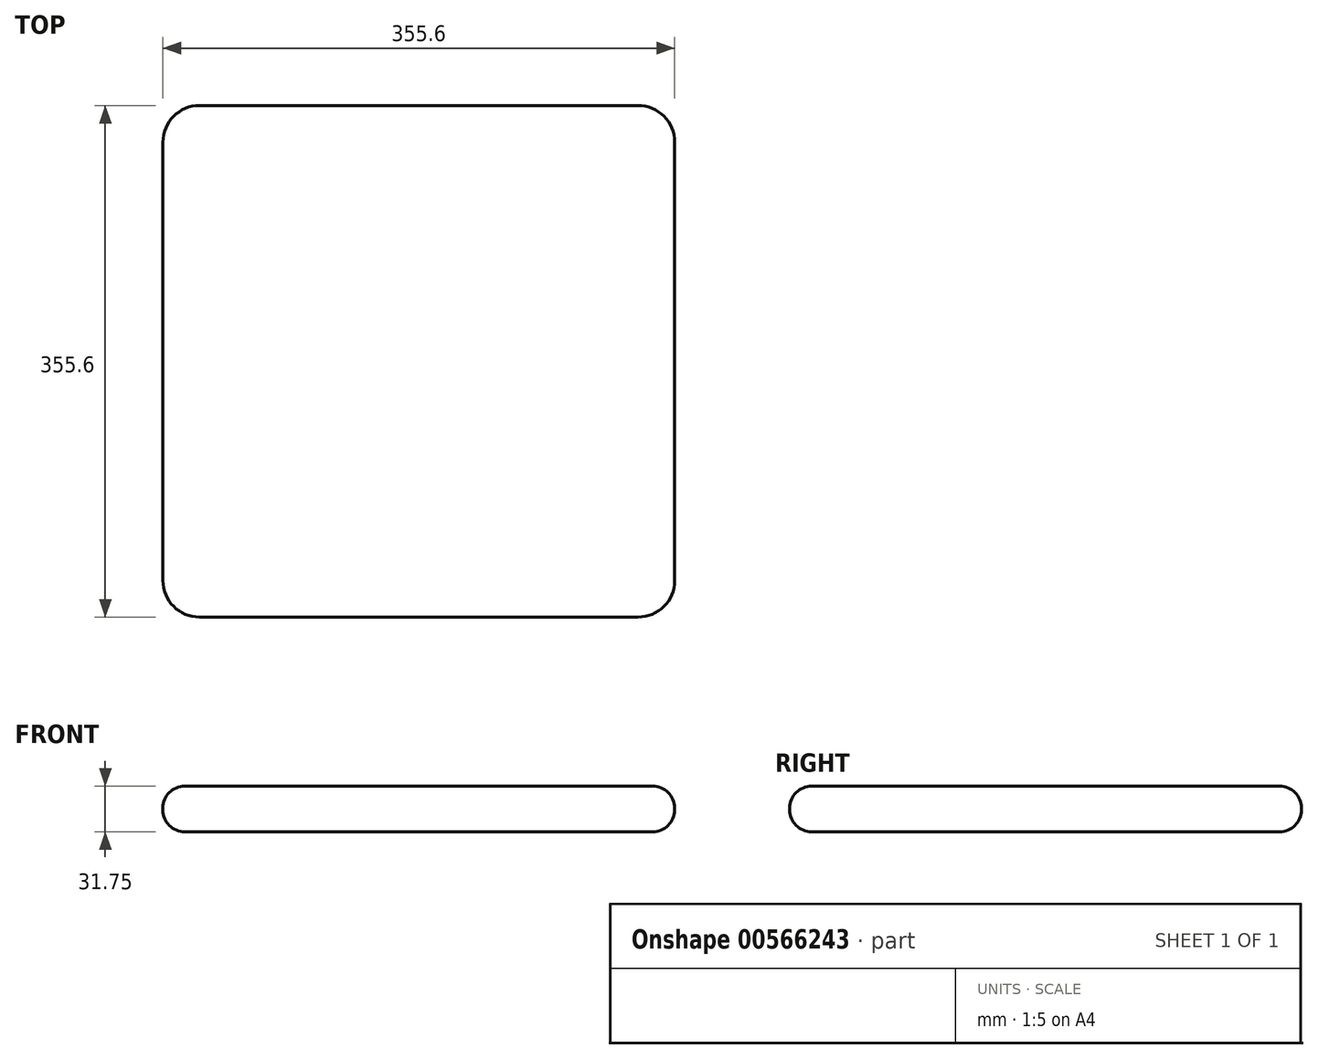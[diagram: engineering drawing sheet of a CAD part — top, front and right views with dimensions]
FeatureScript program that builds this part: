
annotation { "Feature Type Name" : "Feature", "Feature Type Description" : "" }
export const myFeature = defineFeature(function(context is Context, id is Id, definition is map)
    precondition{}
    {
        {
            var Q0;
            Q0=qCreatedBy(makeId("Top.planeOp"),FACE);
            var sketch = newSketch(context, id + "F0", { "sketchPlane" : qUnion([Q0])});
            skLineSegment(sketch, "E0.bottom", {"start": v(-152.4, 177.8) * mm, "end": v(152.4, 177.8) * mm});
            skLineSegment(sketch, "E0.top", {"start": v(-152.4, -177.8) * mm, "end": v(152.4, -177.8) * mm});
            skLineSegment(sketch, "E0.left", {"start": v(-177.8, 152.4) * mm, "end": v(-177.8, -152.4) * mm});
            skLineSegment(sketch, "E0.right", {"start": v(177.8, 152.4) * mm, "end": v(177.8, -152.4) * mm});
            skPoint(sketch, "E0.middle", {"position": v(0, 0) * mm});
            skPoint(sketch, "E1.visualSharp", {"position": v(-177.8, 177.8) * mm});
            skArc(sketch, "E1.filletArc", {"start": v(-152.4, 177.8) * mm, "mid": v(-170.36, 170.36) * mm, "end": v(-177.8, 152.4) * mm});
            skPoint(sketch, "E2.visualSharp", {"position": v(177.8, 177.8) * mm});
            skArc(sketch, "E2.filletArc", {"start": v(177.8, 152.4) * mm, "mid": v(170.36, 170.36) * mm, "end": v(152.4, 177.8) * mm});
            skPoint(sketch, "E3.visualSharp", {"position": v(-177.8, -177.8) * mm});
            skArc(sketch, "E3.filletArc", {"start": v(-177.8, -152.4) * mm, "mid": v(-170.36, -170.36) * mm, "end": v(-152.4, -177.8) * mm});
            skPoint(sketch, "E4.visualSharp", {"position": v(177.8, -177.8) * mm});
            skArc(sketch, "E4.filletArc", {"start": v(152.4, -177.8) * mm, "mid": v(170.36, -170.36) * mm, "end": v(177.8, -152.4) * mm});
            skSolve(sketch);
        }
        {
            var Q0;
            Q0=makeQuery(id+"F0.imprint","IMPRINT",FACE,{"disambiguationData":[TD([[makeQuery(id+"F0.imprint","IMPRINT",EDGE,{"derivedFrom":sQuery(id+"F0.wireOp",EDGE,"E0.bottom")}),-1.0]])]});
            extrude(context, id + "F1", {"entities" : qUnion([Q0]), "depth" : 31.75 * mm, "offsetDistance" : 25.4 * mm});
        }
        {
            var Q0;
            Q0=makeQuery(id+"F1.opExtrude","SWEPT_FACE",FACE,{"disambiguationData":[OSD([sQuery(id+"F0.wireOp",EDGE,"E0.bottom")])]});
            var Q1;
            Q1=makeQuery(id+"F1.opExtrude","CAP_FACE",FACE,{"disambiguationData":[OSD([sQuery(id+"F0.wireOp",EDGE,"E0.bottom"),sQuery(id+"F0.wireOp",EDGE,"E0.top"),sQuery(id+"F0.wireOp",EDGE,"E0.left"),sQuery(id+"F0.wireOp",EDGE,"E0.right"),sQuery(id+"F0.wireOp",EDGE,"E1.filletArc"),sQuery(id+"F0.wireOp",EDGE,"E2.filletArc"),sQuery(id+"F0.wireOp",EDGE,"E3.filletArc"),sQuery(id+"F0.wireOp",EDGE,"E4.filletArc")])],"isStart":false});
            var Q2;
            Q2=makeQuery(id+"F1.opExtrude","CAP_FACE",FACE,{"disambiguationData":[OSD([sQuery(id+"F0.wireOp",EDGE,"E0.bottom"),sQuery(id+"F0.wireOp",EDGE,"E0.top"),sQuery(id+"F0.wireOp",EDGE,"E0.left"),sQuery(id+"F0.wireOp",EDGE,"E0.right"),sQuery(id+"F0.wireOp",EDGE,"E1.filletArc"),sQuery(id+"F0.wireOp",EDGE,"E2.filletArc"),sQuery(id+"F0.wireOp",EDGE,"E3.filletArc"),sQuery(id+"F0.wireOp",EDGE,"E4.filletArc")])],"isStart":true});
            var Q3;
            Q3=makeQuery(id+"F1.opExtrude","SWEPT_FACE",FACE,{"disambiguationData":[OSD([sQuery(id+"F0.wireOp",EDGE,"E0.left")])]});
            var Q4;
            Q4=makeQuery(id+"F1.opExtrude","SWEPT_FACE",FACE,{"disambiguationData":[OSD([sQuery(id+"F0.wireOp",EDGE,"E0.right")])]});
            var Q5;
            Q5=makeQuery(id+"F1.opExtrude","CAP_EDGE",EDGE,{"disambiguationData":[OSD([sQuery(id+"F0.wireOp",EDGE,"E0.bottom")])],"isStart":true});
            var Q6;
            Q6=makeQuery(id+"F1.opExtrude","SWEPT_FACE",FACE,{"disambiguationData":[OSD([sQuery(id+"F0.wireOp",EDGE,"E3.filletArc")])]});
            var Q7;
            Q7=makeQuery(id+"F1.opExtrude","SWEPT_FACE",FACE,{"disambiguationData":[OSD([sQuery(id+"F0.wireOp",EDGE,"E0.top")])]});
            var Q8;
            Q8=makeQuery(id+"F1.opExtrude","SWEPT_FACE",FACE,{"disambiguationData":[OSD([sQuery(id+"F0.wireOp",EDGE,"E2.filletArc")])]});
            var Q9;
            Q9=makeQuery(id+"F1.opExtrude","CAP_EDGE",EDGE,{"disambiguationData":[OSD([sQuery(id+"F0.wireOp",EDGE,"E0.bottom")])],"isStart":false});
            var Q10;
            Q10=makeQuery(id+"F1.opExtrude","SWEPT_FACE",FACE,{"disambiguationData":[OSD([sQuery(id+"F0.wireOp",EDGE,"E1.filletArc")])]});
            var Q11;
            Q11=makeQuery(id+"F1.opExtrude","CAP_EDGE",EDGE,{"disambiguationData":[OSD([sQuery(id+"F0.wireOp",EDGE,"E2.filletArc")])],"isStart":false});
            var Q12;
            Q12=makeQuery(id+"F1.opExtrude","SWEPT_FACE",FACE,{"disambiguationData":[OSD([sQuery(id+"F0.wireOp",EDGE,"E4.filletArc")])]});
            var Q13;
            Q13=makeQuery(id+"F1.opExtrude","CAP_EDGE",EDGE,{"disambiguationData":[OSD([sQuery(id+"F0.wireOp",EDGE,"E0.left")])],"isStart":true});
            var Q14;
            Q14=makeQuery(id+"F1.opExtrude","SWEPT_EDGE",EDGE,{"disambiguationData":[OSD([sQuery(id+"F0.wireOp",EDGE,"E0.top"),sQuery(id+"F0.wireOp",EDGE,"E4.filletArc")])]});
            var Q15;
            Q15=makeQuery(id+"F1.opExtrude","SWEPT_EDGE",EDGE,{"disambiguationData":[OSD([sQuery(id+"F0.wireOp",EDGE,"E0.left"),sQuery(id+"F0.wireOp",EDGE,"E1.filletArc")])]});
            var Q16;
            Q16=makeQuery(id+"F1.opExtrude","CAP_EDGE",EDGE,{"disambiguationData":[OSD([sQuery(id+"F0.wireOp",EDGE,"E0.left")])],"isStart":false});
            var Q17;
            Q17=makeQuery(id+"F1.opExtrude","CAP_EDGE",EDGE,{"disambiguationData":[OSD([sQuery(id+"F0.wireOp",EDGE,"E0.right")])],"isStart":true});
            var Q18;
            Q18=makeQuery(id+"F1.opExtrude","CAP_EDGE",EDGE,{"disambiguationData":[OSD([sQuery(id+"F0.wireOp",EDGE,"E0.right")])],"isStart":false});
            var Q19;
            Q19=makeQuery(id+"F1.opExtrude","SWEPT_EDGE",EDGE,{"disambiguationData":[OSD([sQuery(id+"F0.wireOp",EDGE,"E0.bottom"),sQuery(id+"F0.wireOp",EDGE,"E2.filletArc")])]});
            var Q20;
            Q20=makeQuery(id+"F1.opExtrude","SWEPT_EDGE",EDGE,{"disambiguationData":[OSD([sQuery(id+"F0.wireOp",EDGE,"E0.top"),sQuery(id+"F0.wireOp",EDGE,"E3.filletArc")])]});
            var Q21;
            Q21=makeQuery(id+"F1.opExtrude","SWEPT_EDGE",EDGE,{"disambiguationData":[OSD([sQuery(id+"F0.wireOp",EDGE,"E0.right"),sQuery(id+"F0.wireOp",EDGE,"E2.filletArc")])]});
            var Q22;
            Q22=makeQuery(id+"F1.opExtrude","CAP_EDGE",EDGE,{"disambiguationData":[OSD([sQuery(id+"F0.wireOp",EDGE,"E4.filletArc")])],"isStart":true});
            var Q23;
            Q23=makeQuery(id+"F1.opExtrude","CAP_EDGE",EDGE,{"disambiguationData":[OSD([sQuery(id+"F0.wireOp",EDGE,"E2.filletArc")])],"isStart":true});
            var Q24;
            Q24=makeQuery(id+"F1.opExtrude","CAP_EDGE",EDGE,{"disambiguationData":[OSD([sQuery(id+"F0.wireOp",EDGE,"E0.top")])],"isStart":false});
            var Q25;
            Q25=makeQuery(id+"F1.opExtrude","CAP_EDGE",EDGE,{"disambiguationData":[OSD([sQuery(id+"F0.wireOp",EDGE,"E1.filletArc")])],"isStart":true});
            var Q26;
            Q26=makeQuery(id+"F1.opExtrude","CAP_EDGE",EDGE,{"disambiguationData":[OSD([sQuery(id+"F0.wireOp",EDGE,"E1.filletArc")])],"isStart":false});
            var Q27;
            Q27=makeQuery(id+"F1.opExtrude","CAP_EDGE",EDGE,{"disambiguationData":[OSD([sQuery(id+"F0.wireOp",EDGE,"E3.filletArc")])],"isStart":false});
            var Q28;
            Q28=makeQuery(id+"F1.opExtrude","CAP_EDGE",EDGE,{"disambiguationData":[OSD([sQuery(id+"F0.wireOp",EDGE,"E4.filletArc")])],"isStart":false});
            var Q29;
            Q29=makeQuery(id+"F1.opExtrude","CAP_EDGE",EDGE,{"disambiguationData":[OSD([sQuery(id+"F0.wireOp",EDGE,"E0.top")])],"isStart":true});
            var Q30;
            Q30=makeQuery(id+"F1.opExtrude","SWEPT_EDGE",EDGE,{"disambiguationData":[OSD([sQuery(id+"F0.wireOp",EDGE,"E0.bottom"),sQuery(id+"F0.wireOp",EDGE,"E1.filletArc")])]});
            var Q31;
            Q31=makeQuery(id+"F1.opExtrude","CAP_EDGE",EDGE,{"disambiguationData":[OSD([sQuery(id+"F0.wireOp",EDGE,"E3.filletArc")])],"isStart":true});
            var Q32;
            Q32=makeQuery(id+"F1.opExtrude","SWEPT_EDGE",EDGE,{"disambiguationData":[OSD([sQuery(id+"F0.wireOp",EDGE,"E0.left"),sQuery(id+"F0.wireOp",EDGE,"E3.filletArc")])]});
            var Q33;
            Q33=makeQuery(id+"F1.opExtrude","SWEPT_EDGE",EDGE,{"disambiguationData":[OSD([sQuery(id+"F0.wireOp",EDGE,"E0.right"),sQuery(id+"F0.wireOp",EDGE,"E4.filletArc")])]});
            fillet(context, id + "F2", {"entities" : qUnion([Q0, Q1, Q2, Q3, Q4, Q5, Q6, Q7, Q8, Q9, Q10, Q11, Q12, Q13, Q14, Q15, Q16, Q17, Q18, Q19, Q20, Q21, Q22, Q23, Q24, Q25, Q26, Q27, Q28, Q29, Q30, Q31, Q32, Q33]), "radius" : 15.24 * mm, "tangentPropagation" : true, "allowEdgeOverflow" : false});
        }
    });
